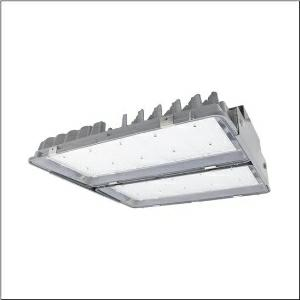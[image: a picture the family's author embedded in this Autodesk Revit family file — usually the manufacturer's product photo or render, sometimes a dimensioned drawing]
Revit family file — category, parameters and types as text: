
# Revit family: highbay_11xtreme_51hf61db4qma
name_source: partatom
category: Lighting Fixtures
units: mm (PartAtom-declared; Revit-internal decimal feet)

## family parameters
Cut with Voids When Loaded = No
Host = Face
Light Source = No
Part Type = Normal
Room Calculation Point = No
Round Connector Dimension = Use Diameter
Shared = No

## types (1)
- --- (1 x LED, 37300 lm, 193.8 W, 4000K)
    Apparent Load = 194 VA
    CIE Flux Codes = 88 96 99 100 100
    Color Rendering = 80
    Color Temperature = 4000K
    Default Elevation = 1800 mm
    Description = Highbay 11Xtreme, high bay luminaire, primary light control with lens, of PMMA, primary optical cover: cover, of toughened safety glass, light emission: direct distribution, primary light characteristic: symmetric, installation type: suspended mounting, surface-mounted, 2x LED module,for 1x 2x LED, rated luminous flux: 36.000lm, luminous efficacy: 178lm/W, light colour: 840, colour temperature: 4000K, control gear: DALI 2 (with two DALI addresses), with cable H07RN-F 5x 1.5mm², mains connection: 220..240V, AC, 50/60Hz, cable length: 1,5m, rated input power: 202W, luminaire housing, of diecast aluminium, coated, silver, length: 595mm, width: 560mm, height: 195mm, protection rating (complete): IP66, insulation class (complete): insulation class I (protective earthing), certification: CE, ENEC, UKCA, protection symbol: D, ball protection: ball impact resistant according to DIN VDE 0710 part 13 (with chain suspension), impact resistance: IK08, permissible operating ambient temperature: -25..+70°C, reducing of maximum allowable ambient temperature of 5°C with ceiling mounting, packaging unit: 1 piece
    Height = 157 mm
    Lamp = 1 x LED
    Lamp Light Flux = 37300 lm
    Lamp Power = 193.8 W
    Lamp count = 1
    Length = 593 mm
    Luminous efficacy = 192 lm/W
    Manufacturer = Siteco
    ModVariant = No
    Model = 51HF61DB4QMA
    Mounting Place = Ceiling
    Mounting Type = Pendant
    Number of Poles = 1
    OnlyDefault = Yes
    Power Factor = 1
    Product Name = Highbay 11Xtreme
    Product group = high bay luminaire
    ProductGroupID = 901
    Protection Class = Protection class I
    Protection Degree = IP 66
    RLX_Detail_Level = 1
    RLX_Emergency_Light_Flux = 0 lm
    RLX_Emergency_Type = 0
    RLX_Emergency_Type_DB = No
    RlxData = <blob elided: 33789 chars, md5=96fb434b>
    Socket = socket
    Standby Power = 0 W
    System Light Flux = 37301 lm
    System Power = 194 W
    Type Comments = factory setting: luminous flux: 100 % | dim-lin: 254 | 648 mA
    Type Image = l_1258340.jpg
    URL = http://relux.com
    VarID = @adj_105047
    Voltage = 0 V
    Weight = 0.00 kg
    Width = 278 mm

## geometry (parser evidence)
native form markers: Blend x4, Sweep x10
no freeform markers — native parametric forms only
